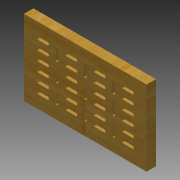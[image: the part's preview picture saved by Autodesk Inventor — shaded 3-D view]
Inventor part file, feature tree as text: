
AUTODESK INVENTOR PART (.ipt)
format: ipt  version: 2014 (Build 180170000, 170)  size: 322,560 bytes
history: native  units: mm
features: extrude x1, sketch x1
ambient origin geometry x8: Origin, YZ Plane, XZ Plane, XY Plane, X Axis, Y Axis, Z Axis, Center Point
bodies: Body1 (feature_tree)
feature tree (2):
  extrude  "Extrusion3"  Depth=80.0mm
  sketch  "Sketch1"  dims[d0=130.0mm d1=80.0mm d5=20.0mm d7=20.0mm d10=20.0mm d14=5.0mm d17=10.0mm d18=3.0mm d28=25.0mm d29=5.0mm d30=10.0mm d32=25.0mm d37=10.0mm d38=3.0mm d40=3.0mm d41=10.0mm d42=10.0mm d44=10.0mm d45=3.0mm d51=15.0mm d52=15.0mm d53=15.0mm d54=15.0mm d55=3.0mm d63=3.0mm d64=3.0mm d65=3.0mm d66=3.0mm d67=3.0mm d68=3.0mm d69=3.0mm d70=3.0mm d71=10.0mm d72=0.0mm]
